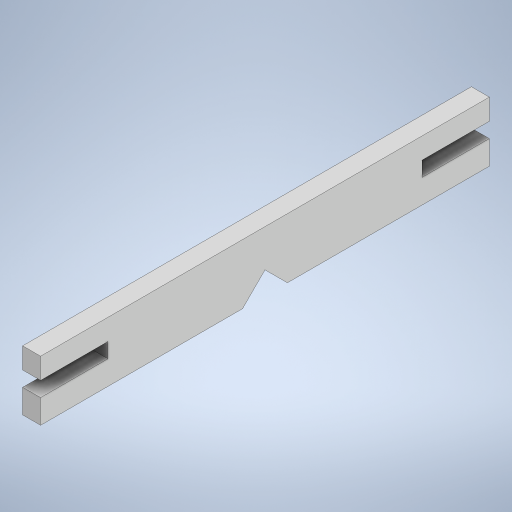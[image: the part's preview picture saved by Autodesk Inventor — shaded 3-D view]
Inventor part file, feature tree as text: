
AUTODESK INVENTOR PART (.ipt)
format: ipt  version: 2023 (Build 270158000, 158)  size: 250,880 bytes
history: native  units: in
note: dims shown in document units (in); Inventor stores cm internally (conversion verified against a paired STEP export)
features: extrude x3, sketch x3
ambient origin geometry x8: Origin, YZ Plane, XZ Plane, XY Plane, X Axis, Y Axis, Z Axis, Center Point
bodies: Solid1 (feature_tree)
feature tree (6):
  extrude  "Extrusion1"  Depth=0.5906in
  extrude  "Extrusion2"  Depth=0.0197in
  extrude  "Extrusion3"  Depth=0.0276in
  sketch  "Sketch1"  dims[d0=0.0787in d1=0.5906in]
  sketch  "Sketch2"  dims[d2=0.0236in d3=0.0in d4=0.0197in]
  sketch  "Sketch3"  dims[d7=0.0236in d8=0.0in d9=0.0276in d10=45.0deg d11=45.0deg d12=0.0591in d13=0.0236in d14=0.0in d15=0.4134in]
